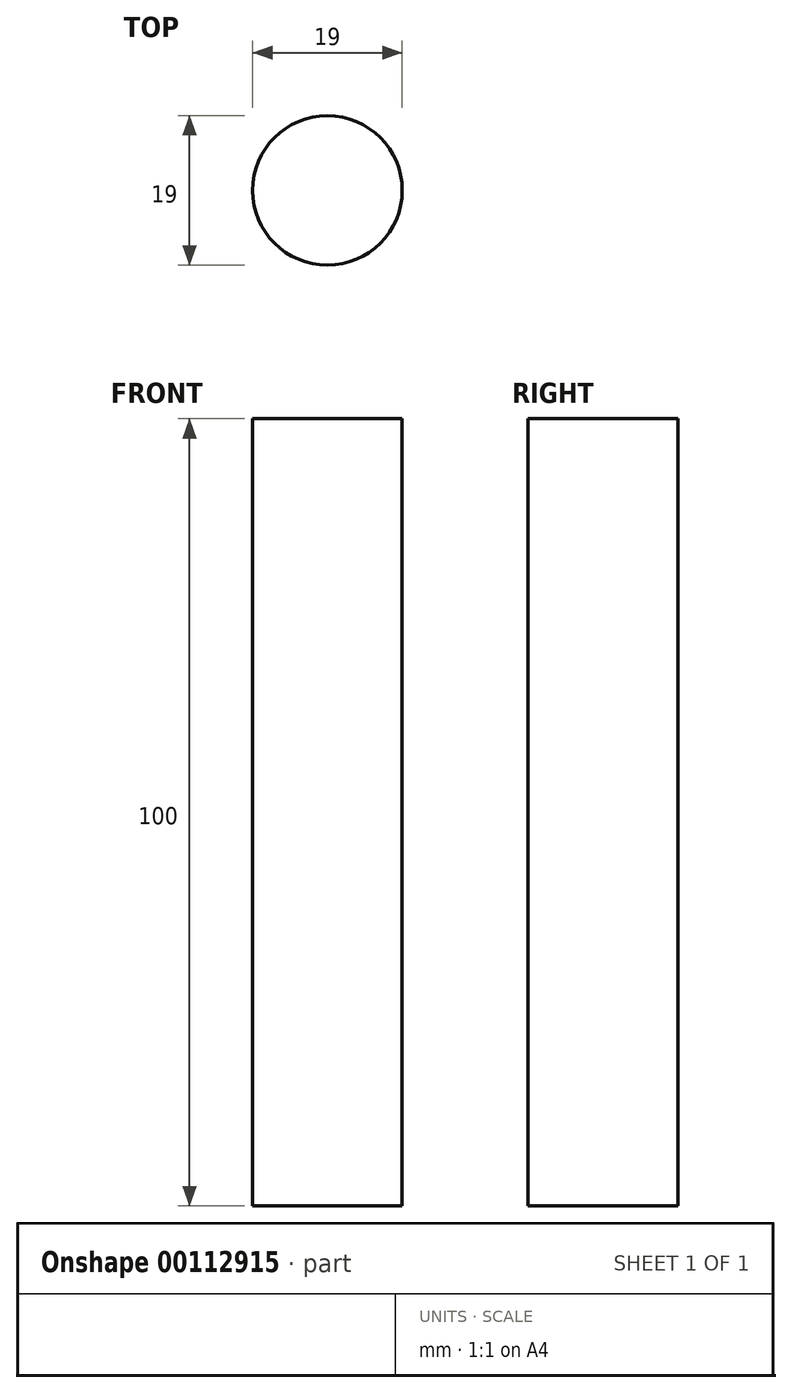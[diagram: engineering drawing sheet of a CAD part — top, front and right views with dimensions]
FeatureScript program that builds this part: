
annotation { "Feature Type Name" : "Feature", "Feature Type Description" : "" }
export const myFeature = defineFeature(function(context is Context, id is Id, definition is map)
    precondition{}
    {
        {
            var Q0;
            Q0=qCreatedBy(makeId("Top.planeOp"),FACE);
            var sketch = newSketch(context, id + "F0", { "sketchPlane" : qUnion([Q0])});
            skCircle(sketch, "E0", {"center": v(0, 0) * mm, "radius": 9.5 * mm});
            skSolve(sketch);
        }
        {
            var Q0;
            Q0 = qSketchRegion(id + "F0", true);
            extrude(context, id + "F1", {"entities" : qUnion([Q0]), "depth" : 100 * mm});
        }
    });
